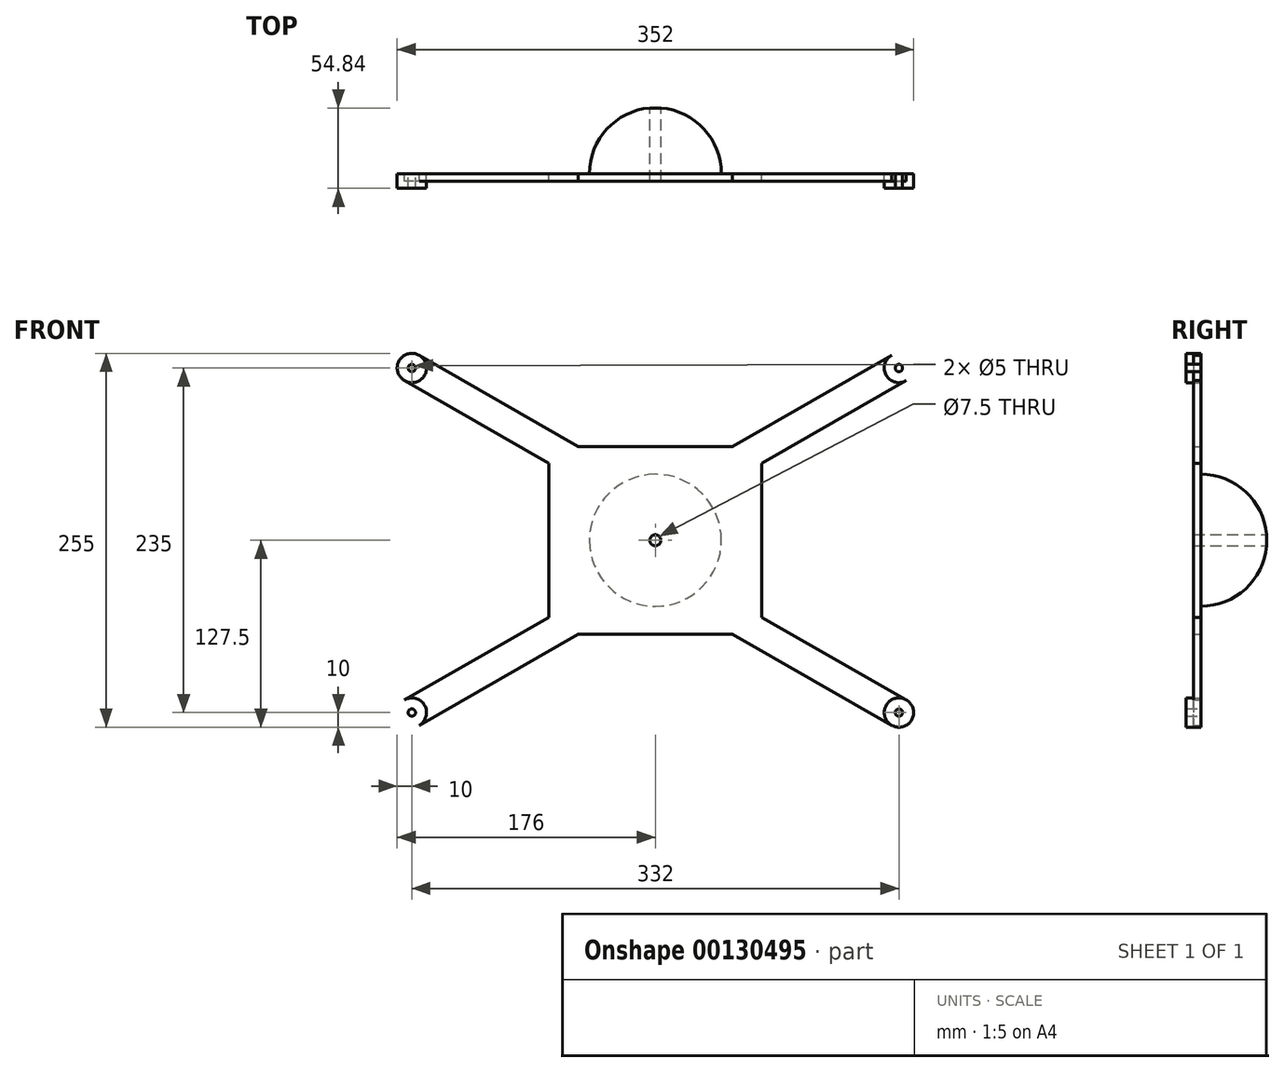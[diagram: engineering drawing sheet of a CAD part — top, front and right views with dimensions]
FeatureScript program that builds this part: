
annotation { "Feature Type Name" : "Feature", "Feature Type Description" : "" }
export const myFeature = defineFeature(function(context is Context, id is Id, definition is map)
    precondition{}
    {
        {
            var Q0;
            Q0=qCreatedBy(makeId("Front.planeOp"),FACE);
            var sketch = newSketch(context, id + "F0", { "sketchPlane" : qUnion([Q0])});
            skPoint(sketch, "E0.middle", {"position": v(0, 0) * mm});
            skCircle(sketch, "E1.MirrorC", {"center": v(-166, -117.5) * mm, "radius": 2.5 * mm});
            skLineSegment(sketch, "E2", {"start": v(-52.5, 64.02) * mm, "end": v(52.5, 64.02) * mm});
            skLineSegment(sketch, "E3", {"start": v(-72.62, 52.5) * mm, "end": v(-72.62, -52.5) * mm});
            skLineSegment(sketch, "E4.MirrorCS", {"start": v(72.62, 52.5) * mm, "end": v(72.62, -52.5) * mm});
            skLineSegment(sketch, "E5.MirrorCS", {"start": v(-52.5, -64.02) * mm, "end": v(52.5, -64.02) * mm});
            skLineSegment(sketch, "E6", {"start": v(-72.62, -52.5) * mm, "end": v(-170.97, -108.82) * mm});
            skLineSegment(sketch, "E7", {"start": v(-52.5, -64.02) * mm, "end": v(-161.03, -126.18) * mm});
            skLineSegment(sketch, "E8.MirrorCS", {"start": v(52.5, -64.02) * mm, "end": v(161.03, -126.18) * mm});
            skLineSegment(sketch, "E9.MirrorCS", {"start": v(72.62, -52.5) * mm, "end": v(170.97, -108.82) * mm});
            skCircle(sketch, "E10.MirrorC", {"center": v(166, -117.5) * mm, "radius": 2.5 * mm});
            skCircle(sketch, "E11.MirrorC", {"center": v(166, 117.5) * mm, "radius": 2.5 * mm});
            skLineSegment(sketch, "E12.MirrorCS", {"start": v(52.5, 64.02) * mm, "end": v(161.03, 126.18) * mm});
            skLineSegment(sketch, "E13.MirrorCS", {"start": v(72.62, 52.5) * mm, "end": v(170.97, 108.82) * mm});
            skLineSegment(sketch, "E14.MirrorCS", {"start": v(-72.62, 52.5) * mm, "end": v(-170.97, 108.82) * mm});
            skCircle(sketch, "E15.MirrorC", {"center": v(-166, 117.5) * mm, "radius": 2.5 * mm});
            skLineSegment(sketch, "E16.MirrorCS", {"start": v(-52.5, 64.02) * mm, "end": v(-161.03, 126.18) * mm});
            skCircle(sketch, "E17", {"center": v(-166, 117.5) * mm, "radius": 10 * mm});
            skCircle(sketch, "E18.MirrorC", {"center": v(-166, -117.5) * mm, "radius": 10 * mm});
            skCircle(sketch, "E19.MirrorC", {"center": v(166, -117.5) * mm, "radius": 10 * mm});
            skCircle(sketch, "E20.MirrorC", {"center": v(166, 117.5) * mm, "radius": 10 * mm});
            skLineSegment(sketch, "E21", {"start": v(-45, 0) * mm, "end": v(45, 0) * mm});
            skArc(sketch, "E22", {"start": v(-45, 0) * mm, "mid": v(0, 45) * mm, "end": v(45, 0) * mm});
            skCircle(sketch, "E23", {"center": v(0, 0) * mm, "radius": 3.75 * mm});
            skSolve(sketch);
        }
        {
            var Q0;
            Q0=makeQuery(id+"F0.imprint","IMPRINT",FACE,{"disambiguationData":[TD([[makeQuery(id+"F0.imprint","IMPRINT",EDGE,{"derivedFrom":sQuery(id+"F0.wireOp",EDGE,"E2")}),-1.0]])]});
            var Q1;
            Q1=makeQuery(id+"F0.imprint","IMPRINT",FACE,{"disambiguationData":[TD([[makeQuery(id+"F0.imprint","IMPRINT",EDGE,{"derivedFrom":sQuery(id+"F0.wireOp",EDGE,"9zifBYsE-L3hb-EYBB-NPHS-OzEXXZjYQfkB")}),1.0]])]});
            var Q2;
            Q2=makeQuery(id+"F0.imprint","IMPRINT",FACE,{"disambiguationData":[TD([[makeQuery(id+"F0.imprint","IMPRINT",EDGE,{"derivedFrom":sQuery(id+"F0.wireOp",EDGE,"E21")}),1.0]])]});
            extrude(context, id + "F1", {"entities" : qUnion([Q0, Q1, Q2]), "depth" : 5 * mm});
        }
        {
            var Q0;
            Q0=makeQuery(id+"F0.imprint","IMPRINT",FACE,{"disambiguationData":[TD([[makeQuery(id+"F0.imprint","IMPRINT",EDGE,{"derivedFrom":sQuery(id+"F0.wireOp",EDGE,"E15.MirrorC")}),-1.0]])]});
            var Q1;
            Q1=makeQuery(id+"F0.imprint","IMPRINT",FACE,{"disambiguationData":[TD([[makeQuery(id+"F0.imprint","IMPRINT",EDGE,{"derivedFrom":sQuery(id+"F0.wireOp",EDGE,"E10.MirrorC")}),-1.0]])]});
            var Q2;
            Q2=makeQuery(id+"F0.imprint","IMPRINT",FACE,{"disambiguationData":[TD([[makeQuery(id+"F0.imprint","IMPRINT",EDGE,{"derivedFrom":sQuery(id+"F0.wireOp",EDGE,"E11.MirrorC")}),1.0]])]});
            var Q3;
            Q3=makeQuery(id+"F0.imprint","IMPRINT",FACE,{"disambiguationData":[TD([[makeQuery(id+"F0.imprint","IMPRINT",EDGE,{"derivedFrom":sQuery(id+"F0.wireOp",EDGE,"E1.MirrorC")}),1.0]])]});
            extrude(context, id + "F2", {"entities" : qUnion([Q0, Q1, Q2, Q3]), "operationType" : NewBodyOperationType.ADD, "depth" : 10 * mm});
        }
        {
            var Q0;
            Q0=makeQuery(id+"F0.imprint","IMPRINT",FACE,{"disambiguationData":[TD([[makeQuery(id+"F0.imprint","IMPRINT",EDGE,{"derivedFrom":sQuery(id+"F0.wireOp",EDGE,"E21")}),1.0]])]});
            var Q1;
            Q1=sQuery(id+"F0.wireOp",EDGE,"E21");
            revolve(context, id + "F3", {"operationType" : NewBodyOperationType.ADD, "entities" : qUnion([Q0]), "axis" : qUnion([Q1]), "revolveType" : RevolveType.ONE_DIRECTION, "oppositeDirection" : true, "angle" : 180 * degree});
        }
        {
            var Q0;
            {var subQ0=sQuery(id+"F0.wireOp",EDGE,"E23");var subQ1=sQuery(id+"F0.wireOp",EDGE,"E21");var subQ2=makeQuery(id+"F0.imprint","INTERSECT",VERTEX,{"disambiguationData":[OD(0.0)],"derivedFrom":[subQ1,subQ0]});Q0=makeQuery(id+"F0.imprint","IMPRINT",FACE,{"disambiguationData":[TD([[makeQuery(id+"F0.imprint","IMPRINT",EDGE,{"disambiguationData":[TD([[subQ2,-1.0]])],"derivedFrom":subQ1}),-1.0]])]});}
            var Q1;
            {var subQ0=sQuery(id+"F0.wireOp",EDGE,"E23");var subQ1=sQuery(id+"F0.wireOp",EDGE,"E21");var subQ2=makeQuery(id+"F0.imprint","INTERSECT",VERTEX,{"disambiguationData":[OD(0.0)],"derivedFrom":[subQ1,subQ0]});Q1=makeQuery(id+"F0.imprint","IMPRINT",FACE,{"disambiguationData":[TD([[makeQuery(id+"F0.imprint","IMPRINT",EDGE,{"disambiguationData":[TD([[subQ2,-1.0]])],"derivedFrom":subQ1}),1.0]])]});}
            extrude(context, id + "F4", {"entities" : qUnion([Q0, Q1]), "operationType" : NewBodyOperationType.REMOVE, "oppositeDirection" : true, "depth" : 45 * mm});
        }
    });
